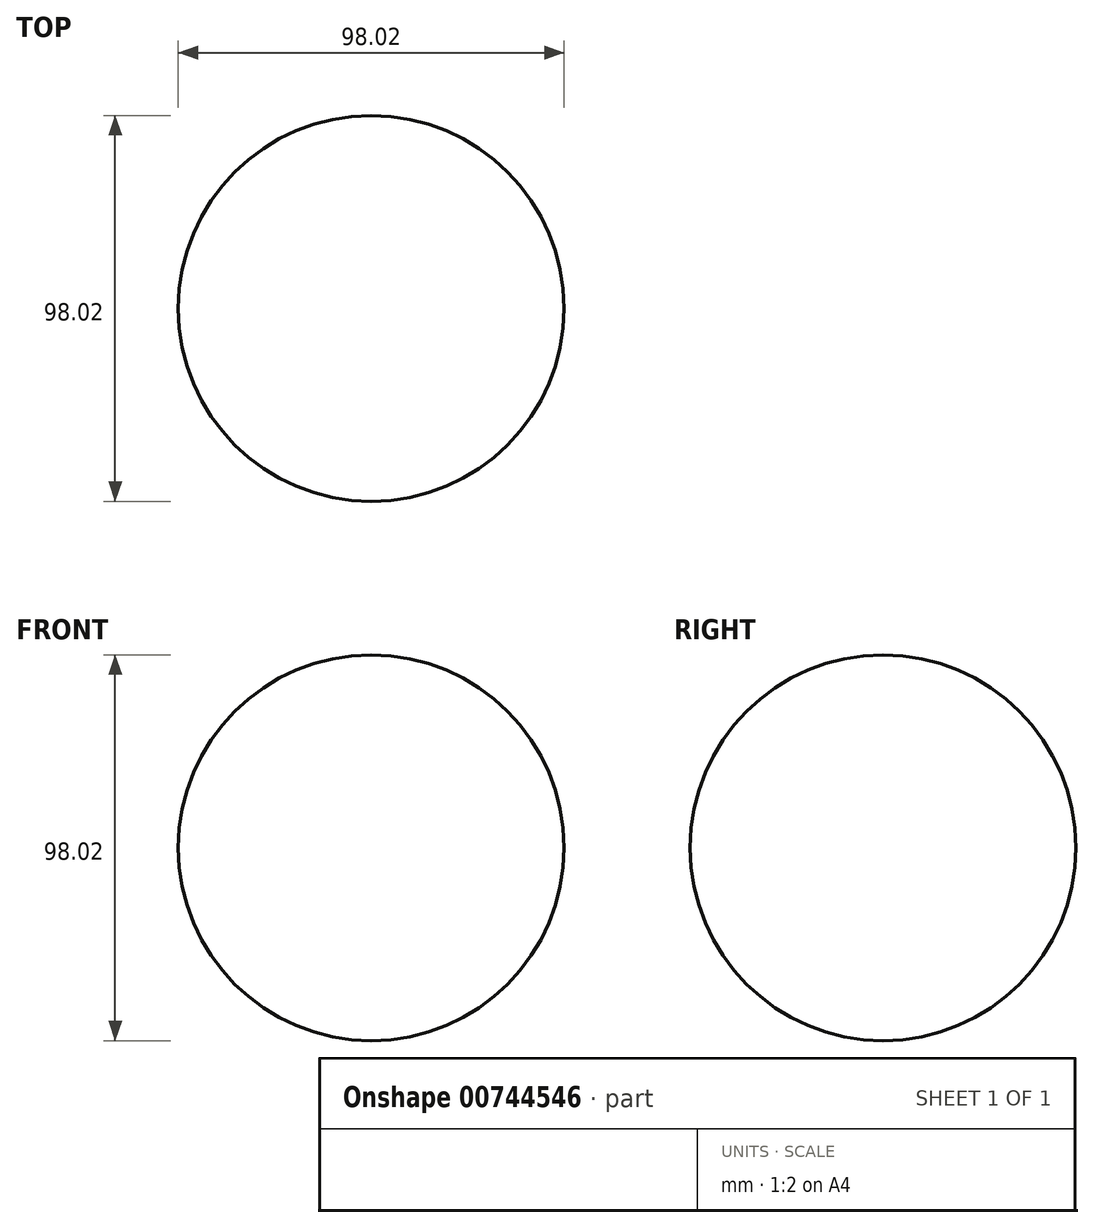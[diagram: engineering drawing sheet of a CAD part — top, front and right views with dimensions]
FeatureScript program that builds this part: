
annotation { "Feature Type Name" : "Feature", "Feature Type Description" : "" }
export const myFeature = defineFeature(function(context is Context, id is Id, definition is map)
    precondition{}
    {
        {
            var Q0;
            Q0=qCreatedBy(makeId("Front.planeOp"),FACE);
            var sketch = newSketch(context, id + "F0", { "sketchPlane" : qUnion([Q0])});
            skArc(sketch, "E0", {"start": v(49.01, 0) * mm, "mid": v(0, 49.01) * mm, "end": v(-49.01, 0) * mm});
            skLineSegment(sketch, "E1", {"start": v(-49.01, 0) * mm, "end": v(49.01, 0) * mm});
            skPoint(sketch, "E2.orphan", {"position": v(-55.76, 0) * mm});
            skSolve(sketch);
        }
        {
            var Q0;
            Q0 = qSketchRegion(id + "F0", true);
            var Q1;
            Q1=sQuery(id+"F0.wireOp",EDGE,"E1");
            revolve(context, id + "F1", {"surfaceOperationType" : NewSurfaceOperationType.NEW, "entities" : qUnion([Q0]), "axis" : qUnion([Q1]), "revolveType" : RevolveType.FULL});
        }
    });
